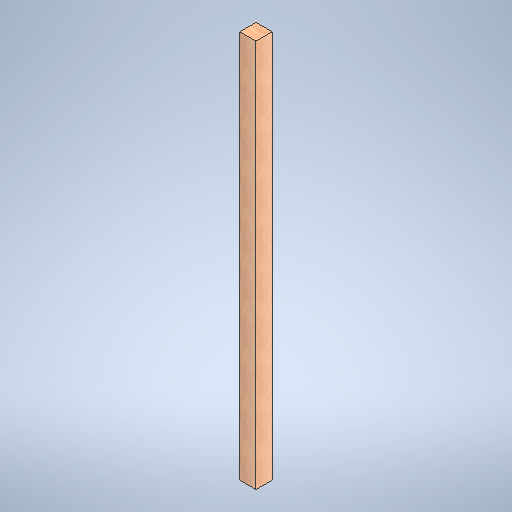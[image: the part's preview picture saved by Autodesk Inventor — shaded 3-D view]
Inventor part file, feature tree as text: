
AUTODESK INVENTOR PART (.ipt)
format: ipt  version: 2025 (Build 290162000, 162)  size: 292,864 bytes
history: native  units: in
note: dims shown in document units (in); Inventor stores cm internally (conversion verified against a paired STEP export)
features: extrude x1, sketch x1
ambient origin geometry x8: Origin, YZ Plane, XZ Plane, XY Plane, X Axis, Y Axis, Z Axis, Center Point
bodies: Solid1 (feature_tree)
feature tree (2):
  extrude  "Extrusion1"  Depth=4.0in
  sketch  "Sketch1"  dims[d0=4.0in d1=4.0in d2=96.0in d3=0.0in d4=0.5in d5=0.0344in d6=0.5in d7=0.0344in]
